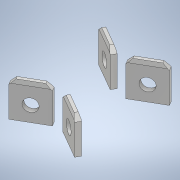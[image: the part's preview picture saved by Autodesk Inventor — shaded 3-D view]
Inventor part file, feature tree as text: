
AUTODESK INVENTOR PART (.ipt)
format: ipt  version: 2022.1 (Build 261234000, 234)  size: 161,792 bytes
history: native  units: mm
features: other x3, reference x3, extrude x2, chamfer x2, sketch x2, pattern_circular x1, mirror x1
ambient origin geometry x8: Origin, YZ Plane, XZ Plane, XY Plane, X Axis, Y Axis, Z Axis, Center Point
bodies: Body1 (feature_tree)
feature tree (14):
  other  "Твердое тело1"
  extrude  "Выдавливание1"  Depth=1.0mm
  chamfer  "Фаска1"  Distance=6.35mm
  chamfer  "Фаска2"  Angle=30.0deg  [1 undecoded]
  extrude  "Выдавливание2"  Depth=12.0mm
  pattern_circular  "Круговой массив1"  [2 undecoded]
  mirror  "Зеркальное отражение1"
  sketch  "Эскиз1"
  reference  "Ссылка1"
  reference  "Ссылка2"
  reference  "Ссылка3"
  sketch  "Эскиз2"
  other  "PS18-16 assy.iam"
  other  "body:1"
note: 3 required parameter values undecoded (feature->parameter linkage not recoverable at this tier; creation-order binding heuristic only, values carry confidence <= 0.55)
